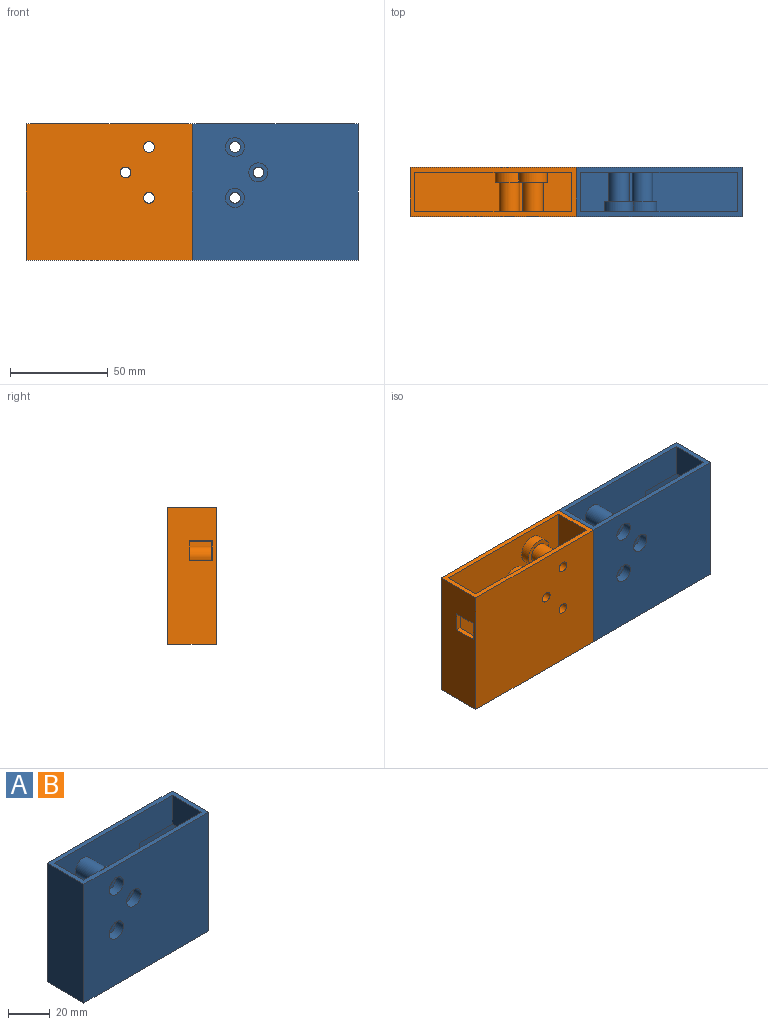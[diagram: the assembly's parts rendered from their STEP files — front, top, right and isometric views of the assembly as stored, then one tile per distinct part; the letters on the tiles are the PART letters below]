
ASSEMBLY  parts=2 mates=1
PART A: 34 faces, bbox 85x25x70 mm
  f0: plane 70x25mm, normal (1,0,0), area 1630mm2, adj f3,f5,f6,f7,f29,f30,f31,f32
  f1: plane 80x67.5mm, normal (0,-1,0), area 4915.2mm2, adj f2,f3,f17,f18,f20,f23,f26,f30
  f2: plane 67.5x20mm, normal (-1,0,0), area 1235mm2, adj f1,f3,f18,f19,f29,f30,f31
  f3: plane 85x25mm, normal (0,0,1), area 525mm2, adj f0,f1,f2,f4,f6,f7,f17,f19
  f4: plane 70x25mm, normal (-1,0,0), area 1750mm2, adj f3,f5,f6,f7
  f5: plane 85x25mm, normal (0,0,-1), area 2125mm2, adj f0,f4,f6,f7
  f6: plane 85x70mm, normal (0,-1,0), area 5726mm2, adj f0,f3,f4,f5,f10,f13,f16
  f7: plane 85x70mm, normal (0,1,0), area 5878.7mm2, adj f0,f3,f4,f5,f8,f11,f14
  f8: cylinder r=2.75mm len=20mm, axis (0,-1,0), area 345.6mm2, adj f7,f9
  f9: plane 9.75x9.75mm, normal (0,-1,0), area 50.9mm2, adj f8,f10
  f10: cylinder r=4.88mm len=9.75mm, axis (0,-1,0), area 153.2mm2, adj f6,f9
  f11: cylinder r=2.75mm len=20mm, axis (0,-1,0), area 345.6mm2, adj f7,f12
  f12: plane 9.75x9.75mm, normal (0,-1,0), area 50.9mm2, adj f11,f13
  f13: cylinder r=4.88mm len=9.75mm, axis (0,-1,0), area 153.2mm2, adj f6,f12
  f14: cylinder r=2.75mm len=20mm, axis (0,-1,0), area 345.6mm2, adj f7,f15
  f15: plane 9.75x9.75mm, normal (0,-1,0), area 50.9mm2, adj f14,f16
  f16: cylinder r=4.88mm len=9.75mm, axis (0,-1,0), area 153.2mm2, adj f6,f15
  f17: plane 67.5x20mm, normal (1,0,0), area 1350mm2, adj f1,f3,f18,f19
  f18: plane 80x20mm, normal (0,0,1), area 1600mm2, adj f1,f2,f17,f19
  f19: plane 80x67.5mm, normal (0,1,0), area 4887.4mm2, adj f2,f3,f17,f18,f22,f25,f28
  f20: cylinder r=5.25mm len=15mm, axis (0,-1,0), area 494.8mm2, adj f1,f21
  f21: plane 14.75x14.75mm, normal (0,1,0), area 84.3mm2, adj f20,f22
  f22: cylinder r=7.38mm len=14.75mm, axis (0,-1,0), area 231.7mm2, adj f19,f21
  f23: cylinder r=5.25mm len=15mm, axis (0,-1,0), area 494.8mm2, adj f1,f24
  f24: plane 14.75x14.75mm, normal (0,1,0), area 84.3mm2, adj f23,f25
  f25: cylinder r=7.38mm len=14.75mm, axis (0,-1,0), area 231.7mm2, adj f19,f24
  f26: cylinder r=5.25mm len=15mm, axis (0,-1,0), area 494.8mm2, adj f1,f27
  f27: plane 14.75x14.75mm, normal (0,1,0), area 84.3mm2, adj f26,f28
  f28: cylinder r=7.38mm len=14.75mm, axis (0,-1,0), area 231.7mm2, adj f19,f27
  f29: plane 10x2.5mm, normal (0,1,0), area 25mm2, adj f0,f2,f30,f31
  f30: plane 25x12mm, normal (0,0,-1), area 41.3mm2, adj f0,f1,f2,f29,f32,f33
  f31: plane 25x12mm, normal (0,0,1), area 41.3mm2, adj f0,f1,f2,f29,f32,f33
  f32: plane 25x10mm, normal (0,-1,0), area 250mm2, adj f0,f30,f31,f33
  f33: plane 10x0.5mm, normal (1,0,0), area 5mm2, adj f1,f30,f31,f32
PART B: same geometry as A
PLACE A t=(-0.21,-0.06,0.08)mm fixed
PLACE B rot(axis=(0,0,1),180deg) t=(-85.21,-0.06,0.08)mm
MATE fastened A.f6 <-> B.f7  axis (0,-1,0) through (-42.71,-12.56,35.08)mm
